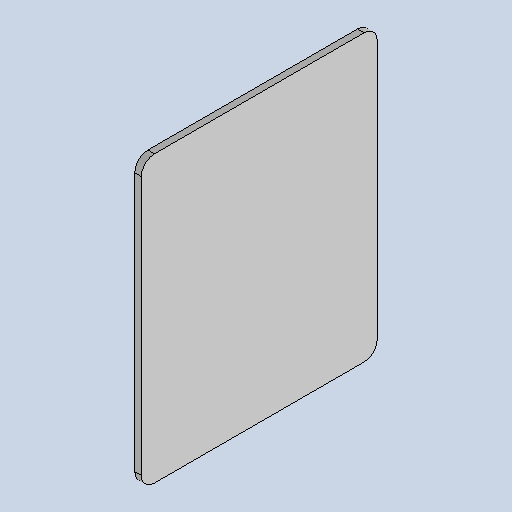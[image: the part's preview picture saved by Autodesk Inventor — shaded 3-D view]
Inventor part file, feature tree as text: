
AUTODESK INVENTOR PART (.ipt)
format: ipt  version: 2025 (Build 290162010, 162A)  size: 120,832 bytes
history: native  units: mm
features: other x2, sheet_metal_op x1, chamfer x1, sketch x1
ambient origin geometry x8: Origin, YZ Plane, XZ Plane, XY Plane, X Axis, Y Axis, Z Axis, Center Point
bodies: Solid1 (feature_tree)
feature tree (5):
  sheet_metal_op  "Face1"
  chamfer  "Corner Round1"
  sketch  "Sketch1"  dims[d0=130.0mm d1=107.582mm d2=3.0mm d3=6.0mm]
  other  "Plate1"
  other  "Definition1"
